# Revit family: P500318-009-30
name_source: partatom
category: Lighting Fixtures
revit_build: Autodesk Revit 2014 (Build: 20130308_1515(x64)
units: mm (PartAtom-declared; Revit-internal decimal feet)

## types (1)
- P500318-009-30
    Apparent Load = 20 VA
    Assembly Code = D5020200
    Color Filter = 16777215
    Connector Description = Lighting Connector
    Default Elevation = 48 "
    Description = Modern minimalism meets the future of industrial style in the Spoke LED Collection 1-Light Brushed Nickel LED Modern Hanging Pendant Light.Sleek rods coated in a beautiful brushed nickel finish anchor the luminous circles for a retro yet contemporary vibe. A slim disk of integrated LEDs casts an ethereal glow that creates a multi-directional wash of even light.
    Dimming Lamp Color Temperature Shift = <None>
    Features = Application: Modern minimalism meets the future of industrial style in the Spoke LED Collection 1-Light Brushed Nickel LED Modern Hanging Pendant Light ideal for any foyer, dining room, kitchen, breakfast nook, entryway, living room, or stairway.
Styles: Perfect for modern, contemporary, and mid-century modern style settings.
Finish: Sleek rods coated in a beautiful brushed nickel finish anchor the luminous circles for a retro yet contemporary vibe.
Materials: Constructed from steel to ensure a long product lifespan.
Glass/Shades: A slim disk of integrated LEDs casts an ethereal glow that creates a multi-directional wash of even light.
Bulbs: For ideal illumination, 1 integrated LED is included (20w). 3000K. 90CRI. 1762 delivered lumens. Dimmable.
Dimensions: Measures 17-3/4-inch diameter by 6-1/2-inch height.
Certifications: cCSAus damp location listed, meets California Title 24 JA8-2019.
Pairs With: Pairs with a variety of Progress Lighting fixtures.
Warranty: Our 5-Year Limited Warranty guarantees your complete satisfaction with your purchase and includes professional after-sales customer service support.
    Fixture distribution = Direct
    Glass = Paint - Hubbell - White Texture
    Gold = Paint - Hubbell - Light Silver
    Height = 10 "
    Housing Material = Paint - Hubbell - Matte White
    Lamp = LED or Medium Base
    Load Classification = Lighting
    Manufacturer = Progress Lighting
    Model = P500318-009-30
    Photometric Web File = generic.ies
    Power Factor = 1
    Product Documentation Link = https://hubbellcdn.com
    Product Link = https://www.hubbell.com
    Square = 10 "
    Support = Paint - Hubbell - Light Silver
    Tilt Angle = -90.00°
    URL = https://www.hubbell.com
    Voltage = 120 V
    Warranty = 1 year Warranty
    Wattage Comments = 20W
    Watts = 20 W

## geometry (parser evidence)
native form markers: Sweep x4
no freeform markers — native parametric forms only
